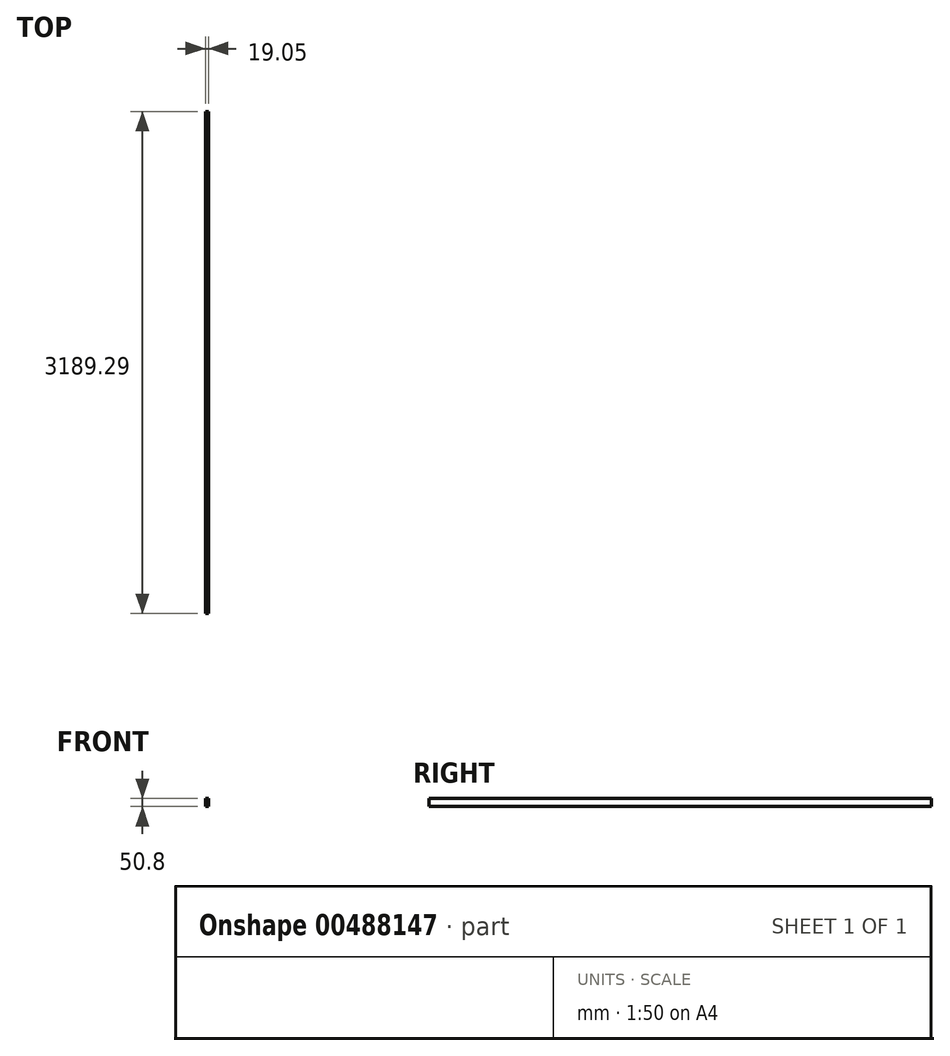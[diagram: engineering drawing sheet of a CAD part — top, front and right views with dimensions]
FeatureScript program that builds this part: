
annotation { "Feature Type Name" : "Feature", "Feature Type Description" : "" }
export const myFeature = defineFeature(function(context is Context, id is Id, definition is map)
    precondition{}
    {
        {
            var Q0;
            Q0=qCreatedBy(makeId("Front.planeOp"),FACE);
            var sketch = newSketch(context, id + "F0", { "sketchPlane" : qUnion([Q0])});
            skLineSegment(sketch, "E0", {"start": v(0, 0) * mm, "end": v(19.05, 0) * mm});
            skLineSegment(sketch, "E1", {"start": v(0, 0) * mm, "end": v(0, -50.8) * mm});
            skLineSegment(sketch, "E2", {"start": v(0, -50.8) * mm, "end": v(19.05, -50.8) * mm});
            skLineSegment(sketch, "E3", {"start": v(19.05, -50.8) * mm, "end": v(19.05, 0) * mm});
            skSolve(sketch);
        }
        {
            var Q0;
            Q0=makeQuery(id+"F0.imprint","IMPRINT",FACE,{"disambiguationData":[TD([[makeQuery(id+"F0.imprint","IMPRINT",EDGE,{"derivedFrom":sQuery(id+"F0.wireOp",EDGE,"E0")}),-1.0]])]});
            extrude(context, id + "F1", {"entities" : qUnion([Q0]), "oppositeDirection" : true, "depth" : 3189.29 * mm, "offsetDistance" : 25.4 * mm});
        }
    });
